# Revit family: Haworth_Masters_Pedestal
name_source: partatom
category: Furniture Systems
revit_build: Autodesk Revit 2018 (Build: 20170223_1515(x64)
units: mm (PartAtom-declared; Revit-internal decimal feet)

## family parameters
Always vertical = Yes
Cut with Voids When Loaded = No
OmniClass Number = 23.40.70.14.64.21
OmniClass Title = Systems Furniture
Part Type = Normal
Room Calculation Point = No
Round Connector Dimension = Use Diameter
Shared = No
Work Plane-Based = No

## types (3) — shared parameters
Actual Width = 15 1/2"
Assembly Code = E2020200
Bar Pull = No
Bar Pull Length = 8 1/16"
Cabinet Finish = Haworth _ Wood _ White Oak
Classic Pull = Yes
Description = Haworth - Masters - Pedestal
Drawer 1 Height = 13"
Drawer 3 Offset = 1/8"
Drawer Finish = Haworth _ Wood _ White Oak
Finger Pull = No
Finished Back = No
Linear Pull = No
Manufacturer = Haworth
Max. Depth = 29"
Max. Height = 28"
Min. Depth = 18"
Min. Height = 21 1/2"
Model = Haworth - Masters - Pedestal
Pull Finish = Haworth _ Metal _ Brushed Aluminum
Revision Number = 3
Size = Verify Final Dim. w/ Haworth
Standard Depths = 18, 21, 23, 29 in
Sustainability Info = http://www.haworth.com
Top Drawer Location = 0"
URL = www.haworth.com
URL - Product = http://www.haworth.com
Warranty = http://www.haworth.com

## per-type parameters (varying)
| type | 3 Drawers | Actual Depth | Actual Height | Attached | Back Edge Of Top | Base Clearance | Box Box File | Box Box File Act | Box File | Custom Size | Depth | File File | File File Act | Legal Width | Letter Width | Mobile | Side Panel Height | Side Panel Width | Top Drawer Height |
| Mobile - Box/File | No | 21" | 21 1/2" | No | 3/4" | 1 7/8" | No | No | Yes | Yes | 23" | No | Yes | Yes | No | Yes | 1 3/4" | 15 1/2" | 6 7/16" |
| Attached - Box/Box/File | Yes | 23" | 28" | Yes | 4" | 0" | Yes | Yes | No | Yes | 21" | No | No | No | Yes | No | 0" | 3/4" | 6 7/16" |
| Attached - File/File | No | 23" | 28" | Yes | 4" | 0" | No | No | No | No | 23" | Yes | Yes | No | Yes | No | 0" | 3/4" | 13" |

## geometry (parser evidence)
native form markers: Sweep x10
no freeform markers — native parametric forms only
